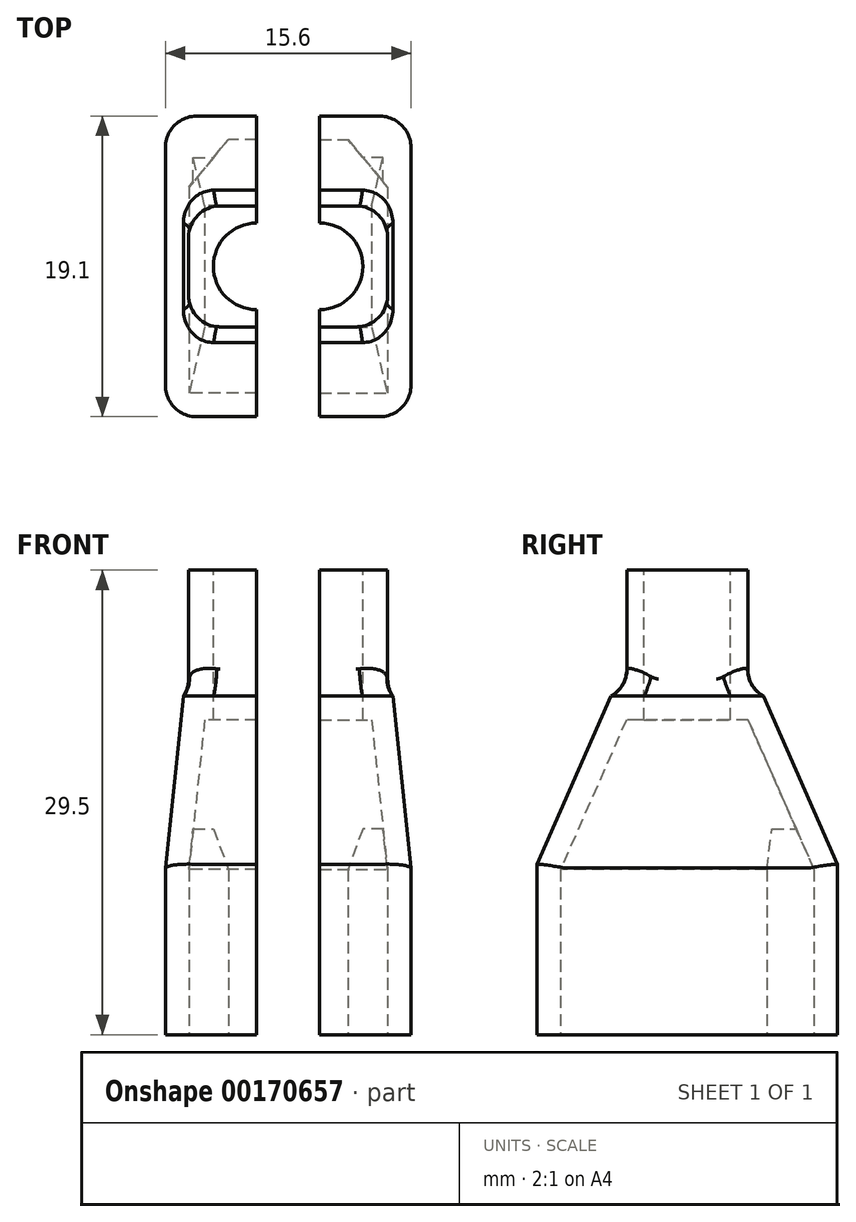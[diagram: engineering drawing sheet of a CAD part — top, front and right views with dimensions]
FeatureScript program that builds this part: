
annotation { "Feature Type Name" : "Feature", "Feature Type Description" : "" }
export const myFeature = defineFeature(function(context is Context, id is Id, definition is map)
    precondition{}
    {
        {
            var Q0;
            Q0=qCreatedBy(makeId("Top.planeOp"),FACE);
            var sketch = newSketch(context, id + "F0", { "sketchPlane" : qUnion([Q0])});
            skLineSegment(sketch, "E0", {"start": v(0, 0) * mm, "end": v(4, 0) * mm, "construction": true});
            skLineSegment(sketch, "E1.bottom", {"start": v(0, 8.05) * mm, "end": v(4.3, 8.05) * mm});
            skLineSegment(sketch, "E1.top", {"start": v(0, -8.05) * mm, "end": v(4.3, -8.05) * mm});
            skLineSegment(sketch, "E1.left", {"start": v(0, 8.05) * mm, "end": v(0, -8.05) * mm});
            skLineSegment(sketch, "E1.right", {"start": v(4.3, 8.05) * mm, "end": v(4.3, -8.05) * mm});
            skSolve(sketch);
        }
        {
            var Q0;
            Q0=makeQuery(id+"F0.imprint","IMPRINT",FACE,{"disambiguationData":[TD([[makeQuery(id+"F0.imprint","IMPRINT",EDGE,{"derivedFrom":sQuery(id+"F0.wireOp",EDGE,"SMyfLETc-uMg7-5ymv-bOYI-8UTbWFQRgBlz.bottom")}),1.0]])]});
            var Q1;
            Q1=makeQuery(id+"F0.imprint","IMPRINT",FACE,{"disambiguationData":[TD([[makeQuery(id+"F0.imprint","IMPRINT",EDGE,{"derivedFrom":sQuery(id+"F0.wireOp",EDGE,"SMyfLETc-uMg7-5ymv-bOYI-8UTbWFQRgBlz.bottom")}),-1.0]])]});
            var Q2;
            Q2=makeQuery(id+"F0.imprint","IMPRINT",FACE,{"disambiguationData":[TD([[makeQuery(id+"F0.imprint","IMPRINT",EDGE,{"derivedFrom":sQuery(id+"F0.wireOp",EDGE,"622bbfad-9d73-4648-9f6b-665f6884d5df.2")}),-1.0]])]});
            var Q3;
            Q3=makeQuery(id+"F0.imprint","IMPRINT",FACE,{"disambiguationData":[TD([[makeQuery(id+"F0.imprint","IMPRINT",EDGE,{"derivedFrom":sQuery(id+"F0.wireOp",EDGE,"E1.bottom")}),-1.0]])]});
            extrude(context, id + "F1", {"entities" : qUnion([Q0, Q1, Q2, Q3]), "depth" : 20 * mm});
        }
        {
            var Q0;
            Q0=makeQuery(id+"F1.opExtrude","SWEPT_FACE",FACE,{"disambiguationData":[OSD([sQuery(id+"F0.wireOp",EDGE,"E1.right")])]});
            var sketch = newSketch(context, id + "F2", { "sketchPlane" : qUnion([Q0])});
            skLineSegment(sketch, "E2", {"start": v(-8.05, 10.5) * mm, "end": v(-3.86, 20) * mm});
            skLineSegment(sketch, "E3", {"start": v(0, 0) * mm, "end": v(0, 20) * mm, "construction": true});
            skLineSegment(sketch, "E4.MirrorCS", {"start": v(8.05, 10.5) * mm, "end": v(3.86, 20) * mm});
            skSolve(sketch);
        }
        {
            var Q0;
            Q0 = qSketchRegion(id + "F2", true);
            var Q1;
            {var subQ0=sQuery(id+"F2.wireOp",EDGE,"E2");Q1=makeQuery(id+"F2.imprint","IMPRINT",FACE,{"disambiguationData":[TD([[makeQuery(id+"F2.imprint","IMPRINT",EDGE,{"derivedFrom":subQ0}),1.0]])]});}
            var Q2;
            {var subQ0=sQuery(id+"F2.wireOp",EDGE,"JT5b9EIc-93qh-jDfn-aFIG-gzKivJDWmNRE");Q2=makeQuery(id+"F2.imprint","IMPRINT",FACE,{"disambiguationData":[TD([[makeQuery(id+"F2.imprint","IMPRINT",EDGE,{"derivedFrom":subQ0}),1.0]])]});}
            var Q3;
            {var subQ0=sQuery(id+"F2.wireOp",EDGE,"E4.MirrorCS");Q3=makeQuery(id+"F2.imprint","IMPRINT",FACE,{"disambiguationData":[TD([[makeQuery(id+"F2.imprint","IMPRINT",EDGE,{"derivedFrom":subQ0}),-1.0]])]});}
            extrude(context, id + "F3", {"entities" : qUnion([Q0, Q1, Q2, Q3]), "operationType" : NewBodyOperationType.REMOVE, "oppositeDirection" : true, "depth" : 25 * mm});
        }
        {
            var Q0;
            Q0=makeQuery(id+"F1.opExtrude","SWEPT_FACE",FACE,{"disambiguationData":[OSD([sQuery(id+"F0.wireOp",EDGE,"E1.top")])]});
            var sketch = newSketch(context, id + "F4", { "sketchPlane" : qUnion([Q0])});
            skLineSegment(sketch, "E5", {"start": v(4.3, 10.5) * mm, "end": v(3.3, 20) * mm});
            skLineSegment(sketch, "E6", {"start": v(3.3, 20) * mm, "end": v(4.3, 20) * mm});
            skLineSegment(sketch, "E7", {"start": v(4.3, 20) * mm, "end": v(4.3, 10.5) * mm});
            skSolve(sketch);
        }
        {
            var Q0;
            Q0=makeQuery(id+"F4.imprint","IMPRINT",FACE,{"disambiguationData":[TD([[makeQuery(id+"F4.imprint","IMPRINT",EDGE,{"derivedFrom":sQuery(id+"F4.wireOp",EDGE,"E5")}),-1.0]])]});
            extrude(context, id + "F5", {"entities" : qUnion([Q0]), "operationType" : NewBodyOperationType.REMOVE, "oppositeDirection" : true, "depth" : 25 * mm});
        }
        {
            var Q0;
            Q0=makeQuery(id+"F1.opExtrude","SWEPT_FACE",FACE,{"disambiguationData":[OSD([sQuery(id+"F0.wireOp",EDGE,"SMyfLETc-uMg7-5ymv-bOYI-8UTbWFQRgBlz.left"),sQuery(id+"F0.wireOp",EDGE,"U1PwO1Vh-qOi0-GEci-TMzN-aw6oTSzoqwUo"),sQuery(id+"F0.wireOp",EDGE,"cVWyJbsA-QPTK-a3z9-Zq1w-ngp8vnv4RipM")])]});
            var Q1;
            Q1=makeQuery(id+"F1.opExtrude","CAP_FACE",FACE,{"disambiguationData":[OSD([sQuery(id+"F0.wireOp",EDGE,"SMyfLETc-uMg7-5ymv-bOYI-8UTbWFQRgBlz.left"),sQuery(id+"F0.wireOp",EDGE,"622bbfad-9d73-4648-9f6b-665f6884d5df.0"),sQuery(id+"F0.wireOp",EDGE,"622bbfad-9d73-4648-9f6b-665f6884d5df.1"),sQuery(id+"F0.wireOp",EDGE,"622bbfad-9d73-4648-9f6b-665f6884d5df.3"),sQuery(id+"F0.wireOp",EDGE,"U1PwO1Vh-qOi0-GEci-TMzN-aw6oTSzoqwUo"),sQuery(id+"F0.wireOp",EDGE,"cVWyJbsA-QPTK-a3z9-Zq1w-ngp8vnv4RipM"),sQuery(id+"F0.wireOp",EDGE,"0CQrDRvL-Til4-6bGE-ws55-BhioIYzxgTuR"),sQuery(id+"F0.wireOp",EDGE,"54htr2mM-ZuSU-8GVf-uHgN-Ixxv2F5IuhkM")])],"isStart":true});
            var Q2;
            Q2=makeQuery(id+"F1.opExtrude","SWEPT_FACE",FACE,{"disambiguationData":[OSD([sQuery(id+"F0.wireOp",EDGE,"E1.left")])]});
            var Q3;
            Q3=makeQuery(id+"F1.opExtrude","CAP_FACE",FACE,{"disambiguationData":[OSD([sQuery(id+"F0.wireOp",EDGE,"E1.bottom"),sQuery(id+"F0.wireOp",EDGE,"E1.top"),sQuery(id+"F0.wireOp",EDGE,"E1.left"),sQuery(id+"F0.wireOp",EDGE,"E1.right")])],"isStart":true});
            shell(context, id + "F6", {"entities" : qUnion([Q0, Q1, Q2, Q3]), "thickness" : 1.5 * mm, "oppositeDirection" : true});
        }
        {
            var Q0;
            Q0=makeQuery(id+"F1.opExtrude","CAP_FACE",FACE,{"disambiguationData":[OSD([sQuery(id+"F0.wireOp",EDGE,"E1.bottom"),sQuery(id+"F0.wireOp",EDGE,"E1.top"),sQuery(id+"F0.wireOp",EDGE,"E1.left"),sQuery(id+"F0.wireOp",EDGE,"E1.right")])],"isStart":false});
            var sketch = newSketch(context, id + "F7", { "sketchPlane" : qUnion([Q0])});
            skArc(sketch, "E8", {"start": v(0, -2.75) * mm, "mid": v(2.75, 0) * mm, "end": v(0, 2.75) * mm});
            skLineSegment(sketch, "E9.0", {"start": v(0, 2.75) * mm, "end": v(0, -2.75) * mm});
            skPoint(sketch, "E10.orphan", {"position": v(0, -4.84) * mm});
            skPoint(sketch, "E11.orphan", {"position": v(0, 4.84) * mm});
            skLineSegment(sketch, "E12", {"start": v(0, 3.84) * mm, "end": v(4.32, 3.84) * mm});
            skLineSegment(sketch, "E13", {"start": v(0, 0) * mm, "end": v(7.3, 0) * mm, "construction": true});
            skPoint(sketch, "E13.endSnap0", {"position": v(4.65, 0) * mm});
            skLineSegment(sketch, "E14", {"start": v(0, -3.84) * mm, "end": v(4.32, -3.84) * mm});
            skLineSegment(sketch, "E15", {"start": v(4.32, -3.84) * mm, "end": v(4.32, 3.84) * mm});
            skSolve(sketch);
        }
        {
            var Q0;
            Q0 = qSketchRegion(id + "F7", true);
            extrude(context, id + "F8", {"entities" : qUnion([Q0]), "operationType" : NewBodyOperationType.REMOVE, "oppositeDirection" : true, "depth" : 25 * mm});
        }
        {
            var Q0;
            {var subQ1=sQuery(id+"F7.wireOp",EDGE,"E8");Q0=makeQuery(id+"F7.imprint","IMPRINT",FACE,{"disambiguationData":[TD([[makeQuery(id+"F7.imprint","IMPRINT",EDGE,{"derivedFrom":subQ1}),-1.0]])]});}
            extrude(context, id + "F9", {"entities" : qUnion([Q0]), "operationType" : NewBodyOperationType.ADD, "depth" : 8 * mm});
        }
        {
            var Q0;
            Q0=makeQuery(id+"F9.opExtrude","SWEPT_EDGE",EDGE,{"disambiguationData":[OSD([sQuery(id+"F7.wireOp",EDGE,"E14"),sQuery(id+"F7.wireOp",EDGE,"E15")])]});
            var Q1;
            Q1=makeQuery(id+"F9.opExtrude","SWEPT_EDGE",EDGE,{"disambiguationData":[OSD([sQuery(id+"F7.wireOp",EDGE,"E12"),sQuery(id+"F7.wireOp",EDGE,"E15")])]});
            fillet(context, id + "F10", {"entities" : qUnion([Q0, Q1]), "radius" : 2 * mm, "tangentPropagation" : true, "allowEdgeOverflow" : false});
        }
        {
            var Q0;
            Q0=makeQuery(id+"F5.boolean.opBoolean","INTERSECT",EDGE,{"derivedFrom":[makeQuery(id+"F3.boolean.opBoolean","COPY",FACE,{"derivedFrom":makeQuery(id+"F3.opExtrude","SWEPT_FACE",FACE,{"disambiguationData":[OSD([sQuery(id+"F2.wireOp",EDGE,"E2")])]})}),makeQuery(id+"F5.opExtrude","SWEPT_FACE",FACE,{"disambiguationData":[OSD([sQuery(id+"F4.wireOp",EDGE,"E5")])]})]});
            var Q1;
            Q1=makeQuery(id+"F1.opExtrude","SWEPT_EDGE",EDGE,{"disambiguationData":[OSD([sQuery(id+"F0.wireOp",EDGE,"E1.top"),sQuery(id+"F0.wireOp",EDGE,"E1.right")])]});
            var Q2;
            Q2=makeQuery(id+"F5.boolean.opBoolean","INTERSECT",EDGE,{"derivedFrom":[makeQuery(id+"F3.boolean.opBoolean","COPY",FACE,{"derivedFrom":makeQuery(id+"F3.opExtrude","SWEPT_FACE",FACE,{"disambiguationData":[OSD([sQuery(id+"F2.wireOp",EDGE,"E4.MirrorCS")])]})}),makeQuery(id+"F5.opExtrude","SWEPT_FACE",FACE,{"disambiguationData":[OSD([sQuery(id+"F4.wireOp",EDGE,"E5")])]})]});
            var Q3;
            Q3=makeQuery(id+"F1.opExtrude","SWEPT_EDGE",EDGE,{"disambiguationData":[OSD([sQuery(id+"F0.wireOp",EDGE,"E1.bottom"),sQuery(id+"F0.wireOp",EDGE,"E1.right")])]});
            fillet(context, id + "F11", {"entities" : qUnion([Q0, Q1, Q2, Q3]), "radius" : 2 * mm, "tangentPropagation" : true, "allowEdgeOverflow" : false});
        }
        {
            var Q0;
            Q0=makeQuery(id+"F1.opExtrude","CAP_FACE",FACE,{"disambiguationData":[OSD([sQuery(id+"F0.wireOp",EDGE,"E1.bottom"),sQuery(id+"F0.wireOp",EDGE,"E1.top"),sQuery(id+"F0.wireOp",EDGE,"E1.left"),sQuery(id+"F0.wireOp",EDGE,"E1.right")])],"isStart":true});
            var sketch = newSketch(context, id + "F12", { "sketchPlane" : qUnion([Q0])});
            skLineSegment(sketch, "E16", {"start": v(1.8, -8.05) * mm, "end": v(4.3, -5.05) * mm});
            skSolve(sketch);
        }
        {
            var Q0;
            Q0 = qSketchRegion(id + "F12", true);
            var Q1;
            {var subQ0=sQuery(id+"F12.wireOp",EDGE,"E16");Q1=makeQuery(id+"F12.imprint","IMPRINT",FACE,{"disambiguationData":[TD([[makeQuery(id+"F12.imprint","IMPRINT",EDGE,{"derivedFrom":subQ0}),-1.0]])]});}
            extrude(context, id + "F13", {"entities" : qUnion([Q0, Q1]), "operationType" : NewBodyOperationType.ADD, "oppositeDirection" : true, "depth" : 13.06 * mm});
        }
        {
            var Q0;
            {var subQ0=sQuery(id+"F7.wireOp",EDGE,"E14");var subQ1=sQuery(id+"F4.wireOp",EDGE,"E5");var subQ2=sQuery(id+"F0.wireOp",EDGE,"E1.left");var subQ4=sQuery(id+"F4.wireOp",EDGE,"E6");Q0=makeQuery(id+"F10.opFillet","BLEND_EDGE",EDGE,{"blendedFrom":[makeQuery(id+"F9.opExtrude","SWEPT_EDGE",EDGE,{"disambiguationData":[OSD([subQ1,subQ4,subQ0])]}),makeQuery(id+"F9.boolean.opBoolean","SPLIT",FACE,{"disambiguationData":[TD([makeQuery(id+"F3.boolean.opBoolean","COPY",FACE,{"derivedFrom":makeQuery(id+"F3.opExtrude","SWEPT_FACE",FACE,{"disambiguationData":[OSD([sQuery(id+"F2.wireOp",EDGE,"E2")])]})})])],"derivedFrom":makeQuery(id+"F1.opExtrude","CAP_FACE",FACE,{"disambiguationData":[OSD([sQuery(id+"F0.wireOp",EDGE,"E1.bottom"),sQuery(id+"F0.wireOp",EDGE,"E1.top"),subQ2,sQuery(id+"F0.wireOp",EDGE,"E1.right")])],"isStart":false})})],"blendedInto":[makeQuery(id+"F9.boolean.opBoolean","SPLIT",FACE,{"disambiguationData":[TD([makeQuery(id+"F3.boolean.opBoolean","COPY",FACE,{"derivedFrom":makeQuery(id+"F3.opExtrude","SWEPT_FACE",FACE,{"disambiguationData":[OSD([sQuery(id+"F2.wireOp",EDGE,"E2")])]})})])],"derivedFrom":makeQuery(id+"F1.opExtrude","CAP_FACE",FACE,{"disambiguationData":[OSD([sQuery(id+"F0.wireOp",EDGE,"E1.bottom"),sQuery(id+"F0.wireOp",EDGE,"E1.top"),subQ2,sQuery(id+"F0.wireOp",EDGE,"E1.right")])],"isStart":false})})]});}
            var Q1;
            {var subQ0=sQuery(id+"F7.wireOp",EDGE,"E12");var subQ1=sQuery(id+"F4.wireOp",EDGE,"E5");var subQ2=sQuery(id+"F0.wireOp",EDGE,"E1.left");var subQ4=sQuery(id+"F4.wireOp",EDGE,"E6");Q1=makeQuery(id+"F10.opFillet","BLEND_EDGE",EDGE,{"blendedFrom":[makeQuery(id+"F9.opExtrude","SWEPT_EDGE",EDGE,{"disambiguationData":[OSD([subQ1,subQ4,subQ0])]}),makeQuery(id+"F9.boolean.opBoolean","SPLIT",FACE,{"disambiguationData":[TD([makeQuery(id+"F3.boolean.opBoolean","COPY",FACE,{"derivedFrom":makeQuery(id+"F3.opExtrude","SWEPT_FACE",FACE,{"disambiguationData":[OSD([sQuery(id+"F2.wireOp",EDGE,"E4.MirrorCS")])]})})])],"derivedFrom":makeQuery(id+"F1.opExtrude","CAP_FACE",FACE,{"disambiguationData":[OSD([sQuery(id+"F0.wireOp",EDGE,"E1.bottom"),sQuery(id+"F0.wireOp",EDGE,"E1.top"),subQ2,sQuery(id+"F0.wireOp",EDGE,"E1.right")])],"isStart":false})})],"blendedInto":[makeQuery(id+"F9.boolean.opBoolean","SPLIT",FACE,{"disambiguationData":[TD([makeQuery(id+"F3.boolean.opBoolean","COPY",FACE,{"derivedFrom":makeQuery(id+"F3.opExtrude","SWEPT_FACE",FACE,{"disambiguationData":[OSD([sQuery(id+"F2.wireOp",EDGE,"E4.MirrorCS")])]})})])],"derivedFrom":makeQuery(id+"F1.opExtrude","CAP_FACE",FACE,{"disambiguationData":[OSD([sQuery(id+"F0.wireOp",EDGE,"E1.bottom"),sQuery(id+"F0.wireOp",EDGE,"E1.top"),subQ2,sQuery(id+"F0.wireOp",EDGE,"E1.right")])],"isStart":false})})]});}
            fillet(context, id + "F14", {"entities" : qUnion([Q0, Q1]), "radius" : 2 * mm, "tangentPropagation" : true, "allowEdgeOverflow" : false});
        }
        {
            var Q0;
            {var subQ1=sQuery(id+"F0.wireOp",EDGE,"E1.left");var subQ2=makeQuery(id+"F1.opExtrude","CAP_EDGE",EDGE,{"disambiguationData":[OSD([subQ1])],"isStart":false});var subQ4=sQuery(id+"F0.wireOp",EDGE,"E1.top");Q0=makeQuery(id+"F9.boolean.opBoolean","MERGE",FACE,{"derivedFrom":[makeQuery(id+"F8.boolean.opBoolean","SPLIT",FACE,{"disambiguationData":[TD([makeQuery(id+"F1.opExtrude","SWEPT_FACE",FACE,{"disambiguationData":[OSD([subQ4])]})])],"derivedFrom":makeQuery(id+"F1.opExtrude","SWEPT_FACE",FACE,{"disambiguationData":[OSD([subQ1])]})}),makeQuery(id+"F9.opExtrude","SWEPT_FACE",FACE,{"disambiguationData":[OSD([subQ1]),TDD([makeQuery(id+"F7.imprint","IMPRINT",EDGE,{"disambiguationData":[TD([[makeQuery(id+"F7.imprint","INTERSECT",VERTEX,{"derivedFrom":[subQ2,sQuery(id+"F7.wireOp",EDGE,"E14")]}),1.0]])],"derivedFrom":subQ2})])]})]});}
            cPlane(context, id + "F15", {"entities" : qUnion([Q0]), "cplaneType" : CPlaneType.OFFSET, "offset" : 2 * mm, "width" : 150 * mm, "height" : 150 * mm});
        }
        {
            var Q0;
            Q0=makeQuery(id+"F1.opExtrude","SWEPT_BODY",BODY,{"disambiguationData":[OSD([sQuery(id+"F0.wireOp",EDGE,"E1.bottom"),sQuery(id+"F0.wireOp",EDGE,"E1.top"),sQuery(id+"F0.wireOp",EDGE,"E1.left"),sQuery(id+"F0.wireOp",EDGE,"E1.right")])]});
            var Q1;
            Q1=qCreatedBy(id+"F15.planeOp",FACE);
            mirror(context, id + "F16", {"entities" : qUnion([Q0]), "mirrorPlane" : qUnion([Q1])});
        }
    });
